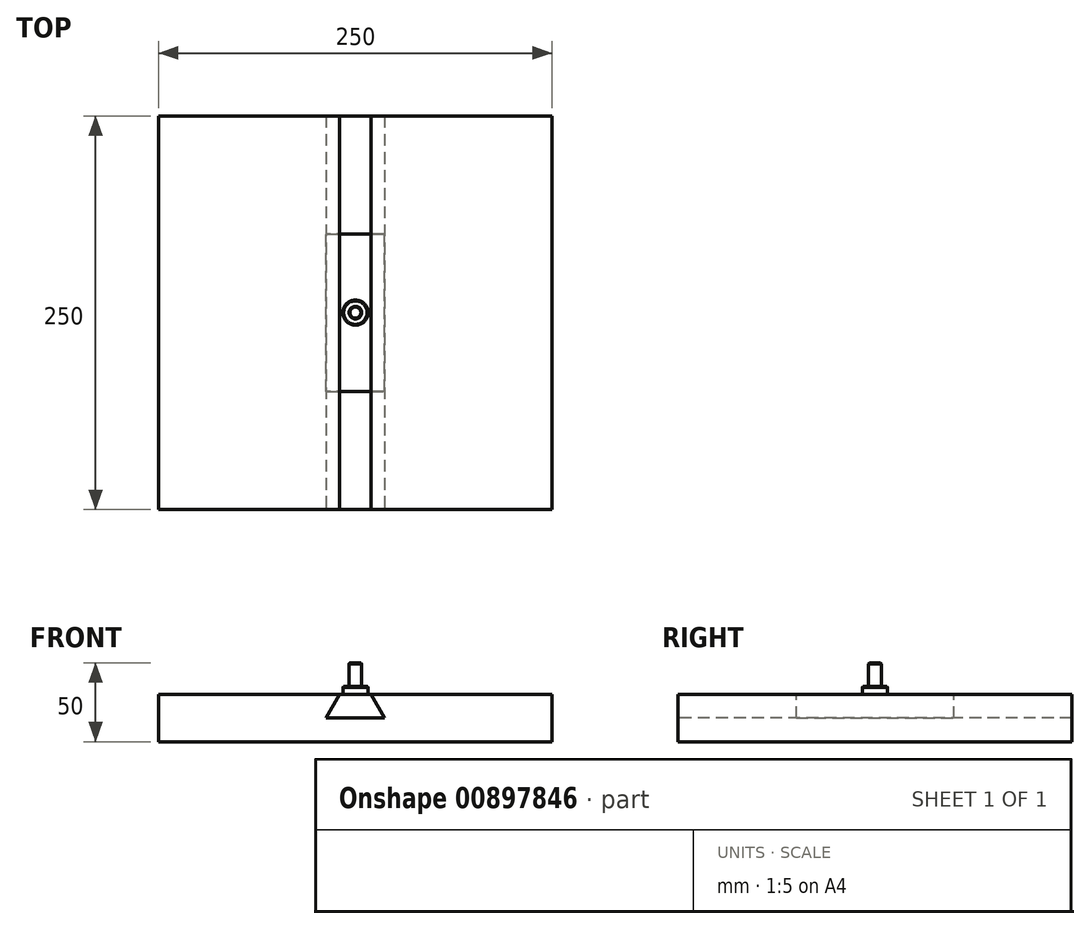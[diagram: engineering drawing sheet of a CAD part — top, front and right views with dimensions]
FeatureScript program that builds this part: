
annotation { "Feature Type Name" : "Feature", "Feature Type Description" : "" }
export const myFeature = defineFeature(function(context is Context, id is Id, definition is map)
    precondition{}
    {
        {
            var Q0;
            Q0=qCreatedBy(makeId("Top.planeOp"),FACE);
            var sketch = newSketch(context, id + "F0", { "sketchPlane" : qUnion([Q0])});
            skLineSegment(sketch, "E0.bottom", {"start": v(125, -125) * mm, "end": v(-125, -125) * mm});
            skLineSegment(sketch, "E0.top", {"start": v(125, 125) * mm, "end": v(-125, 125) * mm});
            skLineSegment(sketch, "E0.left", {"start": v(125, -125) * mm, "end": v(125, 125) * mm});
            skLineSegment(sketch, "E0.right", {"start": v(-125, -125) * mm, "end": v(-125, 125) * mm});
            skPoint(sketch, "E0.middle", {"position": v(0, 0) * mm});
            skSolve(sketch);
        }
        {
            var Q0;
            Q0=makeQuery(id+"F0.imprint","IMPRINT",FACE,{"disambiguationData":[TD([[makeQuery(id+"F0.imprint","IMPRINT",EDGE,{"derivedFrom":sQuery(id+"F0.wireOp",EDGE,"E0.bottom")}),-1.0]])]});
            extrude(context, id + "F1", {"entities" : qUnion([Q0]), "depth" : 30 * mm, "offsetDistance" : 25 * mm});
        }
        {
            var Q0;
            Q0=qCreatedBy(makeId("Front.planeOp"),FACE);
            var sketch = newSketch(context, id + "F2", { "sketchPlane" : qUnion([Q0])});
            skLineSegment(sketch, "E1", {"start": v(-10, 30) * mm, "end": v(10, 30) * mm});
            skLineSegment(sketch, "E2", {"start": v(10, 30) * mm, "end": v(18.66, 15) * mm});
            skLineSegment(sketch, "E3", {"start": v(18.66, 15) * mm, "end": v(-18.66, 15) * mm});
            skLineSegment(sketch, "E4", {"start": v(-18.66, 15) * mm, "end": v(-10, 30) * mm});
            skLineSegment(sketch, "E5", {"start": v(0, 30) * mm, "end": v(0, 15) * mm, "construction": true});
            skSolve(sketch);
        }
        {
            var Q0;
            Q0 = qSketchRegion(id + "F2", true);
            var Q1;
            Q1=makeQuery(id+"F1.opExtrude","SWEPT_FACE",FACE,{"disambiguationData":[OSD([sQuery(id+"F0.wireOp",EDGE,"E0.top")])]});
            extrude(context, id + "F3", {"entities" : qUnion([Q0]), "operationType" : NewBodyOperationType.REMOVE, "oppositeDirection" : true, "depth" : 250 * mm, "endBoundEntityFace" : qUnion([Q1]), "offsetDistance" : 25 * mm, "symmetric" : true});
        }
        {
            var Q0;
            Q0=makeQuery(id+"F2.imprint","IMPRINT",FACE,{"disambiguationData":[TD([[makeQuery(id+"F2.imprint","IMPRINT",EDGE,{"derivedFrom":sQuery(id+"F2.wireOp",EDGE,"E1")}),-1.0]])]});
            extrude(context, id + "F4", {"entities" : qUnion([Q0]), "depth" : 100 * mm, "offsetDistance" : 25 * mm, "symmetric" : true});
        }
        {
            var Q0;
            Q0=makeQuery(id+"F4.opExtrude","SWEPT_FACE",FACE,{"disambiguationData":[OSD([sQuery(id+"F2.wireOp",EDGE,"E1")])]});
            var sketch = newSketch(context, id + "F5", { "sketchPlane" : qUnion([Q0])});
            skPoint(sketch, "E6.0", {"position": v(0, 0) * mm});
            skSolve(sketch);
        }
        {
            var Q0;
            Q0=sQuery(id+"F5.wireOp",VERTEX,"E6.0");
            var Q1;
            Q1=makeQuery(id+"F4.opExtrude","SWEPT_BODY",BODY,{"disambiguationData":[OSD([sQuery(id+"F2.wireOp",EDGE,"E1"),sQuery(id+"F2.wireOp",EDGE,"E2"),sQuery(id+"F2.wireOp",EDGE,"E3"),sQuery(id+"F2.wireOp",EDGE,"E4")])]});
            hole(context, id + "F6", {"style" : HoleStyle.SIMPLE, "endStyle" : HoleEndStyle.BLIND, "holeDiameter" : 8 * mm, "majorDiameter" : 10 * mm, "holeDepth" : 15 * mm, "isTappedThrough" : true, "tappedDepth" : 20.5 * mm, "tapClearance" : 3, "startFromSketch" : true, "locations" : qUnion([Q0]), "scope" : qUnion([Q1])});
        }
        {
            var Q0;
            Q0=makeQuery(id+"F4.opExtrude","SWEPT_FACE",FACE,{"disambiguationData":[OSD([sQuery(id+"F2.wireOp",EDGE,"E3")])]});
            var sketch = newSketch(context, id + "F7", { "sketchPlane" : qUnion([Q0])});
            skCircle(sketch, "E7.0", {"center": v(0, 0) * mm, "radius": 4 * mm});
            skSolve(sketch);
        }
        {
            var Q0;
            Q0 = qSketchRegion(id + "F7", true);
            extrude(context, id + "F8", {"entities" : qUnion([Q0]), "oppositeDirection" : true, "depth" : 35 * mm, "offsetDistance" : 25 * mm});
        }
        {
            var Q0;
            Q0=makeQuery(id+"F4.opExtrude","SWEPT_FACE",FACE,{"disambiguationData":[OSD([sQuery(id+"F2.wireOp",EDGE,"E1")])]});
            var sketch = newSketch(context, id + "F9", { "sketchPlane" : qUnion([Q0])});
            skCircle(sketch, "E8", {"center": v(0, 0) * mm, "radius": 8 * mm});
            skSolve(sketch);
        }
        {
            var Q0;
            Q0 = qSketchRegion(id + "F9", true);
            extrude(context, id + "F10", {"entities" : qUnion([Q0]), "operationType" : NewBodyOperationType.ADD, "depth" : 5 * mm, "offsetDistance" : 25 * mm});
        }
        {
            var Q0;
            Q0=makeQuery(id+"F8.opExtrude","CAP_EDGE",EDGE,{"disambiguationData":[OSD([sQuery(id+"F7.wireOp",EDGE,"E7.0")])],"isStart":false});
            var Q1;
            Q1=makeQuery(id+"F8.opExtrude","CAP_EDGE",EDGE,{"disambiguationData":[OSD([sQuery(id+"F7.wireOp",EDGE,"E7.0")])],"isStart":true});
            var Q2;
            Q2=makeQuery(id+"F10.opExtrude","CAP_EDGE",EDGE,{"disambiguationData":[OSD([sQuery(id+"F9.wireOp",EDGE,"E8")])],"isStart":false});
            var Q3;
            Q3=makeQuery(id+"F10.opExtrude","CAP_EDGE",EDGE,{"disambiguationData":[OSD([sQuery(id+"F9.wireOp",EDGE,"E8")])],"isStart":true});
            chamfer(context, id + "F11", {"entities" : qUnion([Q0, Q1, Q2, Q3]), "width" : 0.5 * mm, "tangentPropagation" : true});
        }
    });
